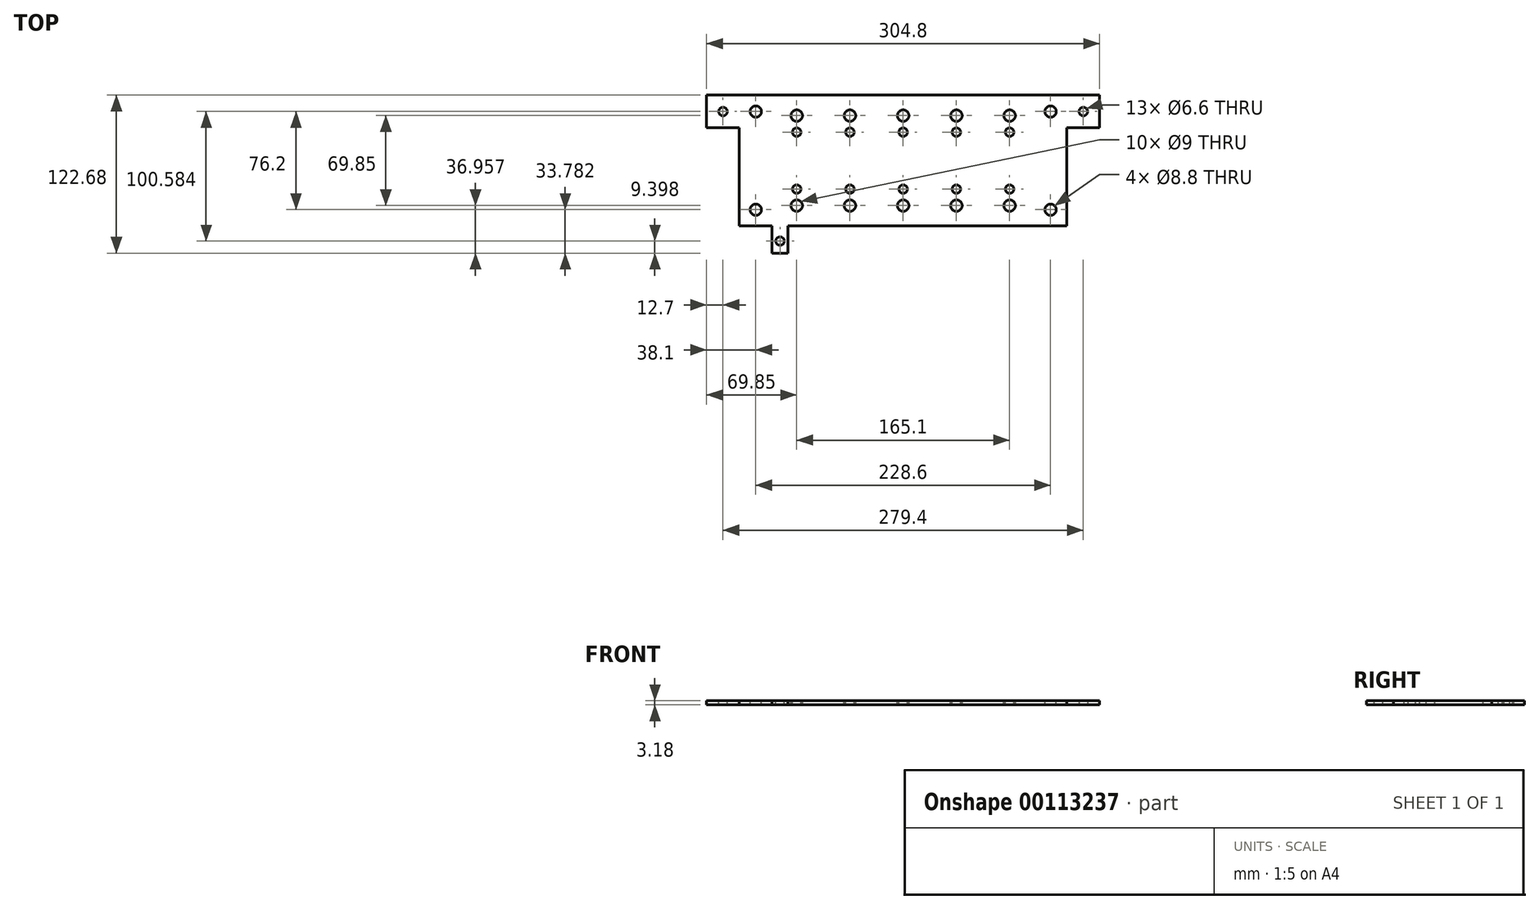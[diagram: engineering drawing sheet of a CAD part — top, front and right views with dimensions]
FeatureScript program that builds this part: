
annotation { "Feature Type Name" : "Feature", "Feature Type Description" : "" }
export const myFeature = defineFeature(function(context is Context, id is Id, definition is map)
    precondition{}
    {
        {
            var Q0;
            Q0=qCreatedBy(makeId("Top.planeOp"),FACE);
            var sketch = newSketch(context, id + "F0", { "sketchPlane" : qUnion([Q0])});
            skLineSegment(sketch, "E0.bottom", {"start": v(-102.08, 88.55) * mm, "end": v(177.32, 88.55) * mm});
            skLineSegment(sketch, "E0.top", {"start": v(-102.08, -13.05) * mm, "end": v(177.32, -13.05) * mm});
            skLineSegment(sketch, "E0.left", {"start": v(-102.08, 88.55) * mm, "end": v(-102.08, -13.05) * mm});
            skLineSegment(sketch, "E0.right", {"start": v(177.32, 88.55) * mm, "end": v(177.32, -13.05) * mm});
            skSolve(sketch);
        }
        {
            var Q0;
            Q0=makeQuery(id+"F0.imprint","IMPRINT",FACE,{"disambiguationData":[TD([[makeQuery(id+"F0.imprint","IMPRINT",EDGE,{"derivedFrom":sQuery(id+"F0.wireOp",EDGE,"E0.bottom")}),-1.0]])]});
            extrude(context, id + "F1", {"entities" : qUnion([Q0]), "depth" : 3.17 * mm});
        }
        {
            var Q0;
            Q0=makeQuery(id+"F1.opExtrude","CAP_FACE",FACE,{"disambiguationData":[OSD([sQuery(id+"F0.wireOp",EDGE,"E0.bottom"),sQuery(id+"F0.wireOp",EDGE,"E0.top"),sQuery(id+"F0.wireOp",EDGE,"E0.left"),sQuery(id+"F0.wireOp",EDGE,"E0.right")])],"isStart":false});
            var sketch = newSketch(context, id + "F2", { "sketchPlane" : qUnion([Q0])});
            skLineSegment(sketch, "E1", {"start": v(-102.08, 63.15) * mm, "end": v(-76.68, 63.15) * mm});
            skLineSegment(sketch, "E2", {"start": v(-76.68, 63.15) * mm, "end": v(-76.68, -13.05) * mm});
            skSolve(sketch);
        }
        {
            var Q0;
            {var subQ0=sQuery(id+"F2.wireOp",EDGE,"E1");Q0=makeQuery(id+"F2.imprint","IMPRINT",FACE,{"disambiguationData":[TD([[makeQuery(id+"F2.imprint","IMPRINT",EDGE,{"derivedFrom":subQ0}),-1.0]])]});}
            extrude(context, id + "F3", {"entities" : qUnion([Q0]), "operationType" : NewBodyOperationType.REMOVE, "endBound" : BoundingType.THROUGH_ALL, "oppositeDirection" : true, "depth" : 25.4 * mm});
        }
        {
            var Q0;
            Q0=makeQuery(id+"F1.opExtrude","CAP_FACE",FACE,{"disambiguationData":[OSD([sQuery(id+"F0.wireOp",EDGE,"E0.bottom"),sQuery(id+"F0.wireOp",EDGE,"E0.top"),sQuery(id+"F0.wireOp",EDGE,"E0.left"),sQuery(id+"F0.wireOp",EDGE,"E0.right")])],"isStart":true});
            var sketch = newSketch(context, id + "F4", { "sketchPlane" : qUnion([Q0])});
            skLineSegment(sketch, "E3.bottom", {"start": v(-51.28, 13.05) * mm, "end": v(-39.09, 13.05) * mm});
            skLineSegment(sketch, "E3.top", {"start": v(-51.28, 34.13) * mm, "end": v(-39.09, 34.13) * mm});
            skLineSegment(sketch, "E3.left", {"start": v(-51.28, 13.05) * mm, "end": v(-51.28, 34.13) * mm});
            skLineSegment(sketch, "E3.right", {"start": v(-39.09, 13.05) * mm, "end": v(-39.09, 34.13) * mm});
            skSolve(sketch);
        }
        {
            var Q0;
            Q0=makeQuery(id+"F4.imprint","IMPRINT",FACE,{"disambiguationData":[TD([[makeQuery(id+"F4.imprint","IMPRINT",EDGE,{"derivedFrom":sQuery(id+"F4.wireOp",EDGE,"E3.bottom")}),1.0]])]});
            var Q1;
            {var subQ8=sQuery(id+"F4.wireOp",EDGE,"E3.bottom");Q1=makeQuery(id+"F4.imprint","IMPRINT",FACE,{"disambiguationData":[TD([[makeQuery(id+"F4.imprint","IMPRINT",EDGE,{"derivedFrom":subQ8}),-1.0]])]});}
            extrude(context, id + "F5", {"entities" : qUnion([Q0, Q1]), "operationType" : NewBodyOperationType.ADD, "oppositeDirection" : true, "depth" : 3.17 * mm});
        }
        {
            var Q0;
            {var subQ0=sQuery(id+"F0.wireOp",EDGE,"E0.right");var subQ1=sQuery(id+"F0.wireOp",EDGE,"E0.left");var subQ2=sQuery(id+"F0.wireOp",EDGE,"E0.top");var subQ3=sQuery(id+"F0.wireOp",EDGE,"E0.bottom");Q0=makeQuery(id+"F5.boolean.opBoolean","MERGE",FACE,{"derivedFrom":[makeQuery(id+"F1.opExtrude","CAP_FACE",FACE,{"disambiguationData":[OSD([subQ3,subQ2,subQ1,subQ0])],"isStart":false}),makeQuery(id+"F5.opExtrude","CAP_FACE",FACE,{"disambiguationData":[OSD([subQ3,subQ2,subQ1,subQ0,sQuery(id+"F2.wireOp",EDGE,"E1"),sQuery(id+"F2.wireOp",EDGE,"E2"),sQuery(id+"F4.wireOp",EDGE,"E3.top"),sQuery(id+"F4.wireOp",EDGE,"E3.left"),sQuery(id+"F4.wireOp",EDGE,"E3.right")])],"isStart":false})]});}
            var sketch = newSketch(context, id + "F6", { "sketchPlane" : qUnion([Q0])});
            skPoint(sketch, "E4", {"position": v(-89.38, 75.85) * mm});
            skSolve(sketch);
        }
        {
            var Q0;
            Q0=sQuery(id+"F6.wireOp",VERTEX,"E4");
            var Q1;
            Q1=makeQuery(id+"F1.opExtrude","SWEPT_BODY",BODY,{"disambiguationData":[OSD([sQuery(id+"F0.wireOp",EDGE,"E0.bottom"),sQuery(id+"F0.wireOp",EDGE,"E0.top"),sQuery(id+"F0.wireOp",EDGE,"E0.left"),sQuery(id+"F0.wireOp",EDGE,"E0.right")])]});
            hole(context, id + "F7", {"style" : HoleStyle.SIMPLE, "endStyle" : HoleEndStyle.THROUGH, "standardTappedOrClearance" : lookupTablePath({ "standard" : "ISO", "fit" : "Normal", "size" : "M6", "type" : "Clearance" }), "standardBlindInLast" : lookupTablePath({ "fit" : "Standard", "standard" : "ISO", "size" : "M6", "type" : "Clearance" }), "holeDiameter" : 6.6 * mm, "locations" : qUnion([Q0]), "scope" : qUnion([Q1]), "isTappedThrough" : true});
        }
        {
            var Q0;
            {var subQ0=sQuery(id+"F0.wireOp",EDGE,"E0.right");var subQ1=sQuery(id+"F0.wireOp",EDGE,"E0.left");var subQ2=sQuery(id+"F0.wireOp",EDGE,"E0.top");var subQ3=sQuery(id+"F0.wireOp",EDGE,"E0.bottom");Q0=makeQuery(id+"F5.boolean.opBoolean","MERGE",FACE,{"derivedFrom":[makeQuery(id+"F1.opExtrude","CAP_FACE",FACE,{"disambiguationData":[OSD([subQ3,subQ2,subQ1,subQ0])],"isStart":false}),makeQuery(id+"F5.opExtrude","CAP_FACE",FACE,{"disambiguationData":[OSD([subQ3,subQ2,subQ1,subQ0,sQuery(id+"F2.wireOp",EDGE,"E1"),sQuery(id+"F2.wireOp",EDGE,"E2"),sQuery(id+"F4.wireOp",EDGE,"E3.top"),sQuery(id+"F4.wireOp",EDGE,"E3.left"),sQuery(id+"F4.wireOp",EDGE,"E3.right")])],"isStart":false})]});}
            var sketch = newSketch(context, id + "F8", { "sketchPlane" : qUnion([Q0])});
            skPoint(sketch, "E5", {"position": v(-63.98, 75.85) * mm});
            skSolve(sketch);
        }
        {
            var Q0;
            Q0=sQuery(id+"F8.wireOp",VERTEX,"E5");
            var Q1;
            Q1=makeQuery(id+"F1.opExtrude","SWEPT_BODY",BODY,{"disambiguationData":[OSD([sQuery(id+"F0.wireOp",EDGE,"E0.bottom"),sQuery(id+"F0.wireOp",EDGE,"E0.top"),sQuery(id+"F0.wireOp",EDGE,"E0.left"),sQuery(id+"F0.wireOp",EDGE,"E0.right")])]});
            hole(context, id + "F9", {"style" : HoleStyle.SIMPLE, "endStyle" : HoleEndStyle.THROUGH, "standardTappedOrClearance" : lookupTablePath({ "standard" : "ISO", "fit" : "Normal", "size" : "M8", "type" : "Clearance" }), "standardBlindInLast" : lookupTablePath({ "fit" : "Standard", "standard" : "ISO", "size" : "M8", "type" : "Clearance" }), "holeDiameter" : 8.8 * mm, "locations" : qUnion([Q0]), "scope" : qUnion([Q1]), "isTappedThrough" : true});
        }
        {
            var Q0;
            {var subQ0=sQuery(id+"F0.wireOp",EDGE,"E0.right");var subQ1=sQuery(id+"F0.wireOp",EDGE,"E0.left");var subQ2=sQuery(id+"F0.wireOp",EDGE,"E0.top");var subQ3=sQuery(id+"F0.wireOp",EDGE,"E0.bottom");Q0=makeQuery(id+"F5.boolean.opBoolean","MERGE",FACE,{"derivedFrom":[makeQuery(id+"F1.opExtrude","CAP_FACE",FACE,{"disambiguationData":[OSD([subQ3,subQ2,subQ1,subQ0])],"isStart":false}),makeQuery(id+"F5.opExtrude","CAP_FACE",FACE,{"disambiguationData":[OSD([subQ3,subQ2,subQ1,subQ0,sQuery(id+"F2.wireOp",EDGE,"E1"),sQuery(id+"F2.wireOp",EDGE,"E2"),sQuery(id+"F4.wireOp",EDGE,"E3.top"),sQuery(id+"F4.wireOp",EDGE,"E3.left"),sQuery(id+"F4.wireOp",EDGE,"E3.right")])],"isStart":false})]});}
            var sketch = newSketch(context, id + "F10", { "sketchPlane" : qUnion([Q0])});
            skLineSegment(sketch, "E6", {"start": v(50.32, 88.55) * mm, "end": v(50.32, -13.05) * mm, "construction": true});
            skLineSegment(sketch, "E7", {"start": v(50.32, 37.75) * mm, "end": v(-76.68, 37.75) * mm, "construction": true});
            skLineSegment(sketch, "E8", {"start": v(50.32, 37.75) * mm, "end": v(177.32, 37.75) * mm, "construction": true});
            skCircle(sketch, "E9.0", {"center": v(-63.98, 75.85) * mm, "radius": 4.4 * mm, "construction": true});
            skCircle(sketch, "E10.MirrorC", {"center": v(-63.98, -0.35) * mm, "radius": 4.4 * mm, "construction": true});
            skCircle(sketch, "E11.MirrorC", {"center": v(164.62, 75.85) * mm, "radius": 4.4 * mm, "construction": true});
            skCircle(sketch, "E12.MirrorC", {"center": v(164.62, -0.35) * mm, "radius": 4.4 * mm, "construction": true});
            skSolve(sketch);
        }
        {
            var Q0;
            Q0=sQuery(id+"F10.wireOp",VERTEX,"E10.MirrorC.center");
            var Q1;
            Q1=sQuery(id+"F10.wireOp",VERTEX,"E12.MirrorC.center");
            var Q2;
            Q2=sQuery(id+"F10.wireOp",VERTEX,"E11.MirrorC.center");
            var Q3;
            Q3=makeQuery(id+"F1.opExtrude","SWEPT_BODY",BODY,{"disambiguationData":[OSD([sQuery(id+"F0.wireOp",EDGE,"E0.bottom"),sQuery(id+"F0.wireOp",EDGE,"E0.top"),sQuery(id+"F0.wireOp",EDGE,"E0.left"),sQuery(id+"F0.wireOp",EDGE,"E0.right")])]});
            hole(context, id + "F11", {"style" : HoleStyle.SIMPLE, "endStyle" : HoleEndStyle.THROUGH, "standardTappedOrClearance" : lookupTablePath({ "standard" : "ISO", "fit" : "Normal", "size" : "M8", "type" : "Clearance" }), "standardBlindInLast" : lookupTablePath({ "fit" : "Standard", "standard" : "ISO", "size" : "M8", "type" : "Clearance" }), "holeDiameter" : 8.8 * mm, "locations" : qUnion([Q0, Q1, Q2]), "scope" : qUnion([Q3]), "isTappedThrough" : true});
        }
        {
            var Q0;
            {var subQ0=sQuery(id+"F0.wireOp",EDGE,"E0.right");var subQ1=sQuery(id+"F0.wireOp",EDGE,"E0.left");var subQ2=sQuery(id+"F0.wireOp",EDGE,"E0.top");var subQ3=sQuery(id+"F0.wireOp",EDGE,"E0.bottom");Q0=makeQuery(id+"F5.boolean.opBoolean","MERGE",FACE,{"derivedFrom":[makeQuery(id+"F1.opExtrude","CAP_FACE",FACE,{"disambiguationData":[OSD([subQ3,subQ2,subQ1,subQ0])],"isStart":false}),makeQuery(id+"F5.opExtrude","CAP_FACE",FACE,{"disambiguationData":[OSD([subQ3,subQ2,subQ1,subQ0,sQuery(id+"F2.wireOp",EDGE,"E1"),sQuery(id+"F2.wireOp",EDGE,"E2"),sQuery(id+"F4.wireOp",EDGE,"E3.top"),sQuery(id+"F4.wireOp",EDGE,"E3.left"),sQuery(id+"F4.wireOp",EDGE,"E3.right")])],"isStart":false})]});}
            var sketch = newSketch(context, id + "F12", { "sketchPlane" : qUnion([Q0])});
            skPoint(sketch, "E13", {"position": v(-45.18, -24.73) * mm});
            skSolve(sketch);
        }
        {
            var Q0;
            Q0=sQuery(id+"F12.wireOp",VERTEX,"E13");
            var Q1;
            Q1=makeQuery(id+"F1.opExtrude","SWEPT_BODY",BODY,{"disambiguationData":[OSD([sQuery(id+"F0.wireOp",EDGE,"E0.bottom"),sQuery(id+"F0.wireOp",EDGE,"E0.top"),sQuery(id+"F0.wireOp",EDGE,"E0.left"),sQuery(id+"F0.wireOp",EDGE,"E0.right")])]});
            hole(context, id + "F13", {"style" : HoleStyle.SIMPLE, "endStyle" : HoleEndStyle.THROUGH, "standardTappedOrClearance" : lookupTablePath({ "standard" : "ISO", "fit" : "Normal", "size" : "M6", "type" : "Clearance" }), "standardBlindInLast" : lookupTablePath({ "fit" : "Standard", "standard" : "ISO", "size" : "M6", "type" : "Clearance" }), "holeDiameter" : 6.6 * mm, "locations" : qUnion([Q0]), "scope" : qUnion([Q1]), "isTappedThrough" : true});
        }
        {
            var Q0;
            Q0=makeQuery(id+"F1.opExtrude","SWEPT_FACE",FACE,{"disambiguationData":[OSD([sQuery(id+"F0.wireOp",EDGE,"E0.right")])]});
            var sketch = newSketch(context, id + "F14", { "sketchPlane" : qUnion([Q0])});
            skLineSegment(sketch, "E14.bottom", {"start": v(88.55, 0) * mm, "end": v(63.15, 0) * mm});
            skLineSegment(sketch, "E14.top", {"start": v(88.55, 3.18) * mm, "end": v(63.15, 3.18) * mm});
            skLineSegment(sketch, "E14.left", {"start": v(88.55, 0) * mm, "end": v(88.55, 3.18) * mm});
            skLineSegment(sketch, "E14.right", {"start": v(63.15, 0) * mm, "end": v(63.15, 3.18) * mm});
            skSolve(sketch);
        }
        {
            var Q0;
            Q0=makeQuery(id+"F14.imprint","IMPRINT",FACE,{"disambiguationData":[TD([[makeQuery(id+"F14.imprint","IMPRINT",EDGE,{"derivedFrom":sQuery(id+"F14.wireOp",EDGE,"E14.bottom")}),-1.0]])]});
            extrude(context, id + "F15", {"entities" : qUnion([Q0]), "operationType" : NewBodyOperationType.ADD, "depth" : 25.4 * mm});
        }
        {
            var Q0;
            {var subQ0=sQuery(id+"F0.wireOp",EDGE,"E0.right");var subQ1=sQuery(id+"F0.wireOp",EDGE,"E0.left");var subQ2=sQuery(id+"F0.wireOp",EDGE,"E0.top");var subQ3=sQuery(id+"F0.wireOp",EDGE,"E0.bottom");Q0=makeQuery(id+"F15.boolean.opBoolean","MERGE",FACE,{"derivedFrom":[makeQuery(id+"F5.boolean.opBoolean","MERGE",FACE,{"derivedFrom":[makeQuery(id+"F1.opExtrude","CAP_FACE",FACE,{"disambiguationData":[OSD([subQ3,subQ2,subQ1,subQ0])],"isStart":true}),makeQuery(id+"F5.opExtrude","CAP_FACE",FACE,{"disambiguationData":[OSD([subQ3,subQ2,subQ1,subQ0,sQuery(id+"F2.wireOp",EDGE,"E1"),sQuery(id+"F2.wireOp",EDGE,"E2"),sQuery(id+"F4.wireOp",EDGE,"E3.top"),sQuery(id+"F4.wireOp",EDGE,"E3.left"),sQuery(id+"F4.wireOp",EDGE,"E3.right")])],"isStart":true})]}),makeQuery(id+"F15.opExtrude","SWEPT_FACE",FACE,{"disambiguationData":[OSD([sQuery(id+"F14.wireOp",EDGE,"E14.bottom")])]})]});}
            var sketch = newSketch(context, id + "F16", { "sketchPlane" : qUnion([Q0])});
            skPoint(sketch, "E15", {"position": v(190.02, -75.85) * mm});
            skSolve(sketch);
        }
        {
            var Q0;
            Q0=sQuery(id+"F16.wireOp",VERTEX,"E15");
            var Q1;
            Q1=makeQuery(id+"F1.opExtrude","SWEPT_BODY",BODY,{"disambiguationData":[OSD([sQuery(id+"F0.wireOp",EDGE,"E0.bottom"),sQuery(id+"F0.wireOp",EDGE,"E0.top"),sQuery(id+"F0.wireOp",EDGE,"E0.left"),sQuery(id+"F0.wireOp",EDGE,"E0.right")])]});
            hole(context, id + "F17", {"style" : HoleStyle.SIMPLE, "endStyle" : HoleEndStyle.THROUGH, "standardTappedOrClearance" : lookupTablePath({ "standard" : "ISO", "fit" : "Normal", "size" : "M6", "type" : "Clearance" }), "standardBlindInLast" : lookupTablePath({ "fit" : "Standard", "standard" : "ISO", "size" : "M6", "type" : "Clearance" }), "holeDiameter" : 6.6 * mm, "locations" : qUnion([Q0]), "scope" : qUnion([Q1]), "isTappedThrough" : true});
        }
        {
            var Q0;
            {var subQ0=sQuery(id+"F0.wireOp",EDGE,"E0.right");var subQ1=sQuery(id+"F0.wireOp",EDGE,"E0.left");var subQ2=sQuery(id+"F0.wireOp",EDGE,"E0.top");var subQ3=sQuery(id+"F0.wireOp",EDGE,"E0.bottom");Q0=makeQuery(id+"F15.boolean.opBoolean","MERGE",FACE,{"derivedFrom":[makeQuery(id+"F5.boolean.opBoolean","MERGE",FACE,{"derivedFrom":[makeQuery(id+"F1.opExtrude","CAP_FACE",FACE,{"disambiguationData":[OSD([subQ3,subQ2,subQ1,subQ0])],"isStart":false}),makeQuery(id+"F5.opExtrude","CAP_FACE",FACE,{"disambiguationData":[OSD([subQ3,subQ2,subQ1,subQ0,sQuery(id+"F2.wireOp",EDGE,"E1"),sQuery(id+"F2.wireOp",EDGE,"E2"),sQuery(id+"F4.wireOp",EDGE,"E3.top"),sQuery(id+"F4.wireOp",EDGE,"E3.left"),sQuery(id+"F4.wireOp",EDGE,"E3.right")])],"isStart":false})]}),makeQuery(id+"F15.opExtrude","SWEPT_FACE",FACE,{"disambiguationData":[OSD([sQuery(id+"F14.wireOp",EDGE,"E14.top")])]})]});}
            var sketch = newSketch(context, id + "F18", { "sketchPlane" : qUnion([Q0])});
            skCircle(sketch, "E16.0", {"center": v(-63.98, 75.85) * mm, "radius": 4.4 * mm});
            skCircle(sketch, "E17.0", {"center": v(164.62, 75.85) * mm, "radius": 4.4 * mm});
            skLineSegment(sketch, "E18", {"start": v(-76.68, 72.68) * mm, "end": v(-32.23, 72.68) * mm, "construction": true});
            skLineSegment(sketch, "E19", {"start": v(-32.23, 72.68) * mm, "end": v(9.04, 72.68) * mm, "construction": true});
            skLineSegment(sketch, "E20", {"start": v(9.04, 72.68) * mm, "end": v(50.32, 72.68) * mm, "construction": true});
            skLineSegment(sketch, "E21", {"start": v(50.32, 72.68) * mm, "end": v(91.6, 72.68) * mm, "construction": true});
            skLineSegment(sketch, "E22", {"start": v(91.6, 72.68) * mm, "end": v(132.87, 72.68) * mm, "construction": true});
            skLineSegment(sketch, "E23", {"start": v(132.87, 72.68) * mm, "end": v(177.32, 72.68) * mm, "construction": true});
            skPoint(sketch, "E24", {"position": v(-32.23, 72.68) * mm});
            skPoint(sketch, "E25", {"position": v(9.04, 72.68) * mm});
            skPoint(sketch, "E26", {"position": v(50.32, 72.68) * mm});
            skPoint(sketch, "E27", {"position": v(91.6, 72.68) * mm});
            skPoint(sketch, "E28", {"position": v(132.87, 72.68) * mm});
            skPoint(sketch, "E29", {"position": v(-32.23, 59.88) * mm});
            skPoint(sketch, "E30", {"position": v(9.04, 59.88) * mm});
            skPoint(sketch, "E31", {"position": v(50.32, 59.88) * mm});
            skPoint(sketch, "E32", {"position": v(91.6, 59.88) * mm});
            skPoint(sketch, "E33", {"position": v(132.87, 59.88) * mm});
            skPoint(sketch, "E34", {"position": v(-32.23, 15.63) * mm});
            skPoint(sketch, "E35", {"position": v(9.04, 15.63) * mm});
            skPoint(sketch, "E36", {"position": v(50.32, 15.63) * mm});
            skPoint(sketch, "E37", {"position": v(91.6, 15.63) * mm});
            skPoint(sketch, "E38", {"position": v(132.87, 15.63) * mm});
            skPoint(sketch, "E39", {"position": v(-32.23, 2.83) * mm});
            skPoint(sketch, "E40", {"position": v(9.04, 2.83) * mm});
            skPoint(sketch, "E41", {"position": v(50.32, 2.83) * mm});
            skPoint(sketch, "E42", {"position": v(91.6, 2.83) * mm});
            skPoint(sketch, "E43", {"position": v(132.87, 2.83) * mm});
            skLineSegment(sketch, "E44", {"start": v(-32.23, 2.83) * mm, "end": v(-32.23, 15.63) * mm, "construction": true});
            skLineSegment(sketch, "E45", {"start": v(-32.23, 59.88) * mm, "end": v(-32.23, 72.68) * mm, "construction": true});
            skLineSegment(sketch, "E46", {"start": v(50.32, 72.68) * mm, "end": v(50.32, 88.55) * mm, "construction": true});
            skLineSegment(sketch, "E47", {"start": v(50.32, 2.83) * mm, "end": v(50.32, -13.05) * mm, "construction": true});
            skSolve(sketch);
        }
        {
            var Q0;
            Q0=sQuery(id+"F18.wireOp",VERTEX,"E24");
            var Q1;
            Q1=sQuery(id+"F18.wireOp",VERTEX,"E25");
            var Q2;
            Q2=sQuery(id+"F18.wireOp",VERTEX,"E26");
            var Q3;
            Q3=sQuery(id+"F18.wireOp",VERTEX,"E27");
            var Q4;
            Q4=sQuery(id+"F18.wireOp",VERTEX,"E28");
            var Q5;
            Q5=sQuery(id+"F18.wireOp",VERTEX,"E43");
            var Q6;
            Q6=sQuery(id+"F18.wireOp",VERTEX,"E42");
            var Q7;
            Q7=sQuery(id+"F18.wireOp",VERTEX,"E41");
            var Q8;
            Q8=sQuery(id+"F18.wireOp",VERTEX,"E40");
            var Q9;
            Q9=sQuery(id+"F18.wireOp",VERTEX,"E39");
            var Q10;
            Q10=makeQuery(id+"F1.opExtrude","SWEPT_BODY",BODY,{"disambiguationData":[OSD([sQuery(id+"F0.wireOp",EDGE,"E0.bottom"),sQuery(id+"F0.wireOp",EDGE,"E0.top"),sQuery(id+"F0.wireOp",EDGE,"E0.left"),sQuery(id+"F0.wireOp",EDGE,"E0.right")])]});
            hole(context, id + "F19", {"style" : HoleStyle.SIMPLE, "endStyle" : HoleEndStyle.THROUGH, "holeDiameter" : 9 * mm, "locations" : qUnion([Q0, Q1, Q2, Q3, Q4, Q5, Q6, Q7, Q8, Q9]), "scope" : qUnion([Q10]), "isTappedThrough" : true});
        }
        {
            var Q0;
            Q0=sQuery(id+"F18.wireOp",VERTEX,"E29");
            var Q1;
            Q1=sQuery(id+"F18.wireOp",VERTEX,"E30");
            var Q2;
            Q2=sQuery(id+"F18.wireOp",VERTEX,"E31");
            var Q3;
            Q3=sQuery(id+"F18.wireOp",VERTEX,"E32");
            var Q4;
            Q4=sQuery(id+"F18.wireOp",VERTEX,"E33");
            var Q5;
            Q5=sQuery(id+"F18.wireOp",VERTEX,"E38");
            var Q6;
            Q6=sQuery(id+"F18.wireOp",VERTEX,"E37");
            var Q7;
            Q7=sQuery(id+"F18.wireOp",VERTEX,"E36");
            var Q8;
            Q8=sQuery(id+"F18.wireOp",VERTEX,"E35");
            var Q9;
            Q9=sQuery(id+"F18.wireOp",VERTEX,"E34");
            var Q10;
            Q10=makeQuery(id+"F1.opExtrude","SWEPT_BODY",BODY,{"disambiguationData":[OSD([sQuery(id+"F0.wireOp",EDGE,"E0.bottom"),sQuery(id+"F0.wireOp",EDGE,"E0.top"),sQuery(id+"F0.wireOp",EDGE,"E0.left"),sQuery(id+"F0.wireOp",EDGE,"E0.right")])]});
            hole(context, id + "F20", {"style" : HoleStyle.SIMPLE, "endStyle" : HoleEndStyle.THROUGH, "standardTappedOrClearance" : lookupTablePath({ "standard" : "ISO", "fit" : "Normal", "size" : "M6", "type" : "Clearance" }), "standardBlindInLast" : lookupTablePath({ "fit" : "Standard", "standard" : "ISO", "size" : "M6", "type" : "Clearance" }), "holeDiameter" : 6.6 * mm, "locations" : qUnion([Q0, Q1, Q2, Q3, Q4, Q5, Q6, Q7, Q8, Q9]), "scope" : qUnion([Q10]), "isTappedThrough" : true});
        }
    });
